FCSTD DOCUMENT  (FreeCAD 0.21R33771 (Git))
Label: bettie body design 1
License: All rights reserved
LicenseURL: http://en.wikipedia.org/wiki/All_rights_reserved
objects: Sketcher::SketchObject×1
note: 1 computed .brp shape members not serialized (recipe doc carries the construction recipe); baked Part::Feature solids carry a one-line shape summary decoded from their .brp

FEATURE [Sketcher::SketchObject] Sketch
  FullyConstrained = false
  sketch-geometry (4):
    g0: LineSegment StartX=10 StartY=-45.8582 StartZ=0 EndX=-104.07 EndY=-45.8582 EndZ=0
    g1: LineSegment StartX=-104.07 StartY=-45.8582 StartZ=0 EndX=18.8051 EndY=230.124 EndZ=0
    g2: LineSegment StartX=18.8051 StartY=230.124 StartZ=0 EndX=-69.7776 EndY=230.124 EndZ=0
    g3: LineSegment StartX=18.8051 StartY=230.124 StartZ=0 EndX=-99.9713 EndY=230.124 EndZ=0
  constraints (8):
    c: Horizontal(g0)
    c: Coincident(g1,g0)
    c: Distance(g1) = 302.1
    c: Angle(g0,g1) = 1.15192
    c: Coincident(g2,g1)
    c: Horizontal(g2)
    c: Coincident(g3,g1)
    c: Horizontal(g3)
